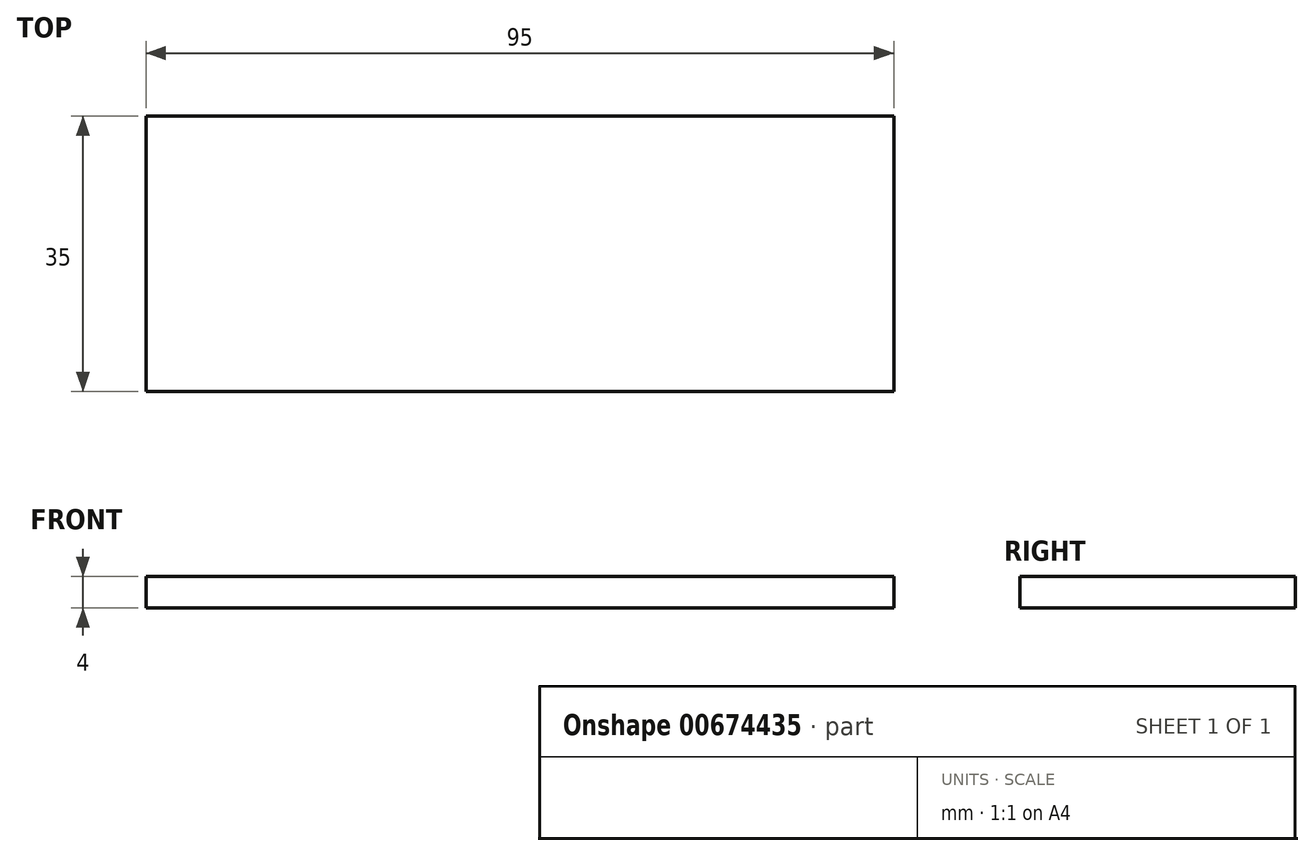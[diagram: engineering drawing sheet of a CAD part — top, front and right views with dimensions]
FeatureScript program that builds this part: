
annotation { "Feature Type Name" : "Feature", "Feature Type Description" : "" }
export const myFeature = defineFeature(function(context is Context, id is Id, definition is map)
    precondition{}
    {
        {
            var Q0;
            Q0=qCreatedBy(makeId("Top.planeOp"),FACE);
            var sketch = newSketch(context, id + "F0", { "sketchPlane" : qUnion([Q0])});
            skLineSegment(sketch, "E0.bottom", {"start": v(0, 0) * mm, "end": v(-95, 0) * mm});
            skLineSegment(sketch, "E0.top", {"start": v(0, 35) * mm, "end": v(-95, 35) * mm});
            skLineSegment(sketch, "E0.left", {"start": v(0, 0) * mm, "end": v(0, 35) * mm});
            skLineSegment(sketch, "E0.right", {"start": v(-95, 0) * mm, "end": v(-95, 35) * mm});
            skSolve(sketch);
        }
        {
            var Q0;
            Q0=makeQuery(id+"F0.imprint","IMPRINT",FACE,{"disambiguationData":[TD([[makeQuery(id+"F0.imprint","IMPRINT",EDGE,{"derivedFrom":sQuery(id+"F0.wireOp",EDGE,"E0.bottom")}),-1.0]])]});
            extrude(context, id + "F1", {"entities" : qUnion([Q0]), "depth" : 4 * mm, "offsetDistance" : 25.4 * mm});
        }
    });
